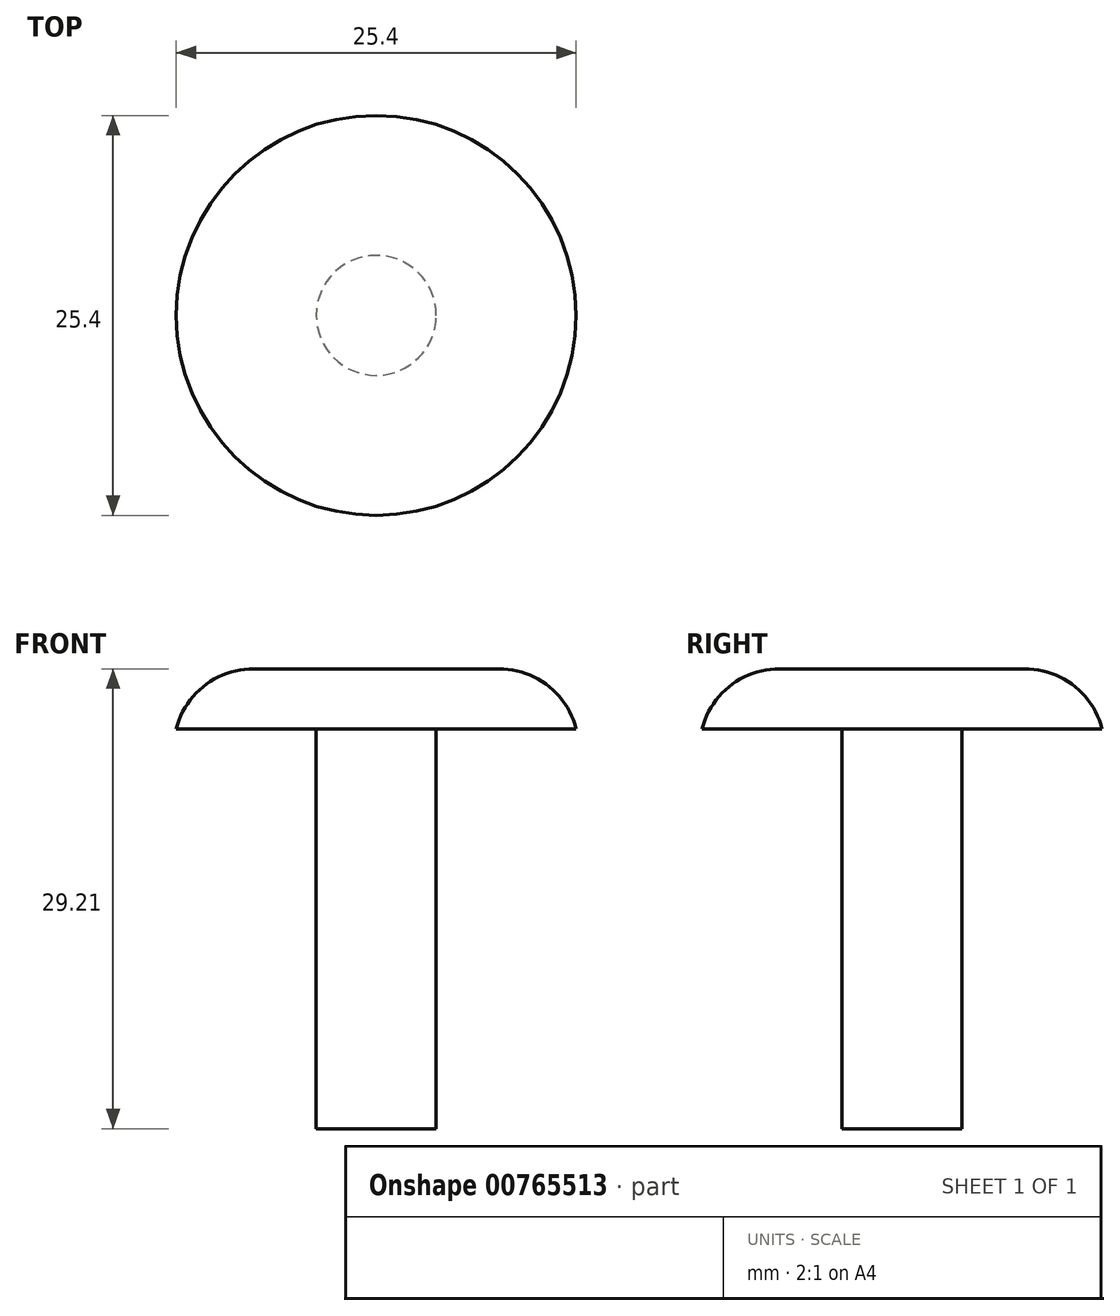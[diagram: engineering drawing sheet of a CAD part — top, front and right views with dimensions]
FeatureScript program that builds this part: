
annotation { "Feature Type Name" : "Feature", "Feature Type Description" : "" }
export const myFeature = defineFeature(function(context is Context, id is Id, definition is map)
    precondition{}
    {
        {
            var Q0;
            Q0=qCreatedBy(makeId("Top.planeOp"),FACE);
            var sketch = newSketch(context, id + "F0", { "sketchPlane" : qUnion([Q0])});
            skCircle(sketch, "E0", {"center": v(0, 0) * mm, "radius": 3.8 * mm});
            skSolve(sketch);
        }
        {
            var Q0;
            Q0 = qSketchRegion(id + "F0", true);
            extrude(context, id + "F1", {"entities" : qUnion([Q0]), "depth" : 25.4 * mm, "offsetDistance" : 25.4 * mm});
        }
        {
            var Q0;
            Q0=makeQuery(id+"F1.opExtrude","CAP_FACE",FACE,{"disambiguationData":[OSD([sQuery(id+"F0.wireOp",EDGE,"E0")])],"isStart":false});
            var sketch = newSketch(context, id + "F2", { "sketchPlane" : qUnion([Q0])});
            skCircle(sketch, "E1", {"center": v(0, 0) * mm, "radius": 6.35 * mm});
            skCircle(sketch, "E2", {"center": v(0, 0) * mm, "radius": 12.7 * mm});
            skSolve(sketch);
        }
        {
            var Q0;
            Q0=makeQuery(id+"F2.imprint","IMPRINT",FACE,{"disambiguationData":[TD([[makeQuery(id+"F2.imprint","IMPRINT",EDGE,{"derivedFrom":sQuery(id+"F2.wireOp",EDGE,"E1")}),1.0]])]});
            var Q1;
            Q1=makeQuery(id+"F2.imprint","IMPRINT",FACE,{"disambiguationData":[TD([[makeQuery(id+"F2.imprint","IMPRINT",EDGE,{"derivedFrom":makeQuery(id+"F1.opExtrude","CAP_EDGE",EDGE,{"disambiguationData":[OSD([sQuery(id+"F0.wireOp",EDGE,"E0")])],"isStart":false})}),1.0]])]});
            extrude(context, id + "F3", {"entities" : qUnion([Q0, Q1]), "operationType" : NewBodyOperationType.ADD, "depth" : 3.8 * mm, "offsetDistance" : 25.4 * mm});
        }
        {
            var Q0;
            Q0=makeQuery(id+"F2.imprint","IMPRINT",FACE,{"disambiguationData":[TD([[makeQuery(id+"F2.imprint","IMPRINT",EDGE,{"derivedFrom":sQuery(id+"F2.wireOp",EDGE,"E1")}),-1.0]])]});
            extrude(context, id + "F4", {"entities" : qUnion([Q0]), "operationType" : NewBodyOperationType.ADD, "depth" : 3.8 * mm, "offsetDistance" : 25.4 * mm});
        }
        {
            var Q0;
            Q0=makeQuery(id+"F4.opExtrude","CAP_EDGE",EDGE,{"disambiguationData":[OSD([sQuery(id+"F2.wireOp",EDGE,"E2")])],"isStart":false});
            fillet(context, id + "F5", {"entities" : qUnion([Q0]), "radius" : 5.08 * mm, "tangentPropagation" : true, "allowEdgeOverflow" : false});
        }
    });
